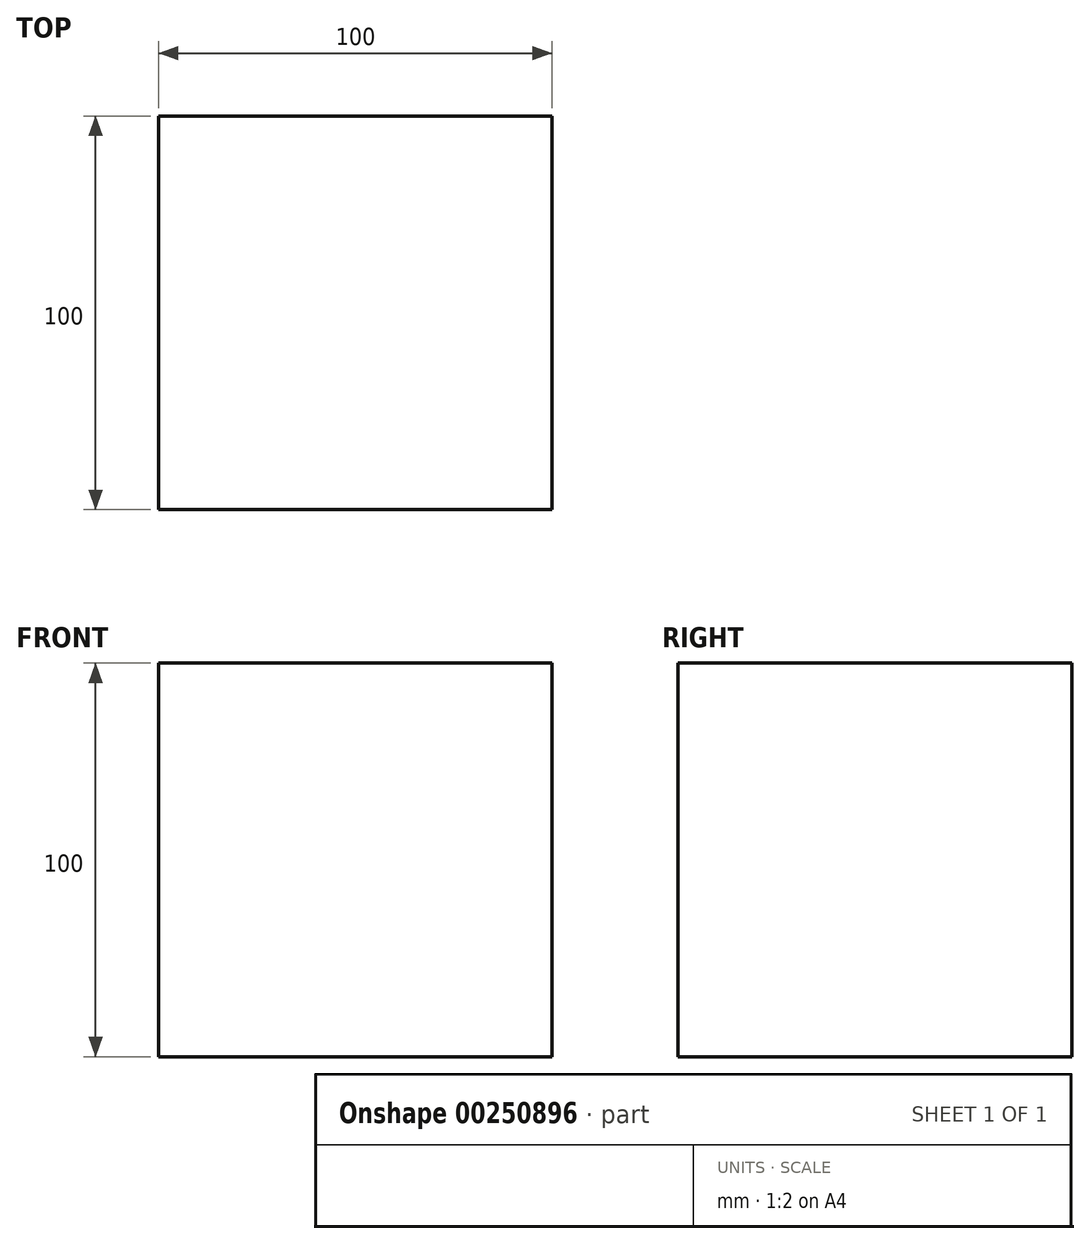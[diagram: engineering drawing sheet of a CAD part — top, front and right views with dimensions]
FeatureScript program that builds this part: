
annotation { "Feature Type Name" : "Feature", "Feature Type Description" : "" }
export const myFeature = defineFeature(function(context is Context, id is Id, definition is map)
    precondition{}
    {
        {
            var Q0;
            Q0=qCreatedBy(makeId("Front.planeOp"),FACE);
            var sketch = newSketch(context, id + "F0", { "sketchPlane" : qUnion([Q0])});
            skLineSegment(sketch, "E0.bottom", {"start": v(50, 50) * mm, "end": v(-50, 50) * mm});
            skLineSegment(sketch, "E0.top", {"start": v(50, -50) * mm, "end": v(-50, -50) * mm});
            skLineSegment(sketch, "E0.left", {"start": v(50, 50) * mm, "end": v(50, -50) * mm});
            skLineSegment(sketch, "E0.right", {"start": v(-50, 50) * mm, "end": v(-50, -50) * mm});
            skPoint(sketch, "E0.middle", {"position": v(0, 0) * mm});
            skSolve(sketch);
        }
        {
            var Q0;
            Q0 = qSketchRegion(id + "F0", true);
            extrude(context, id + "F1", {"entities" : qUnion([Q0]), "depth" : 100 * mm});
        }
    });
